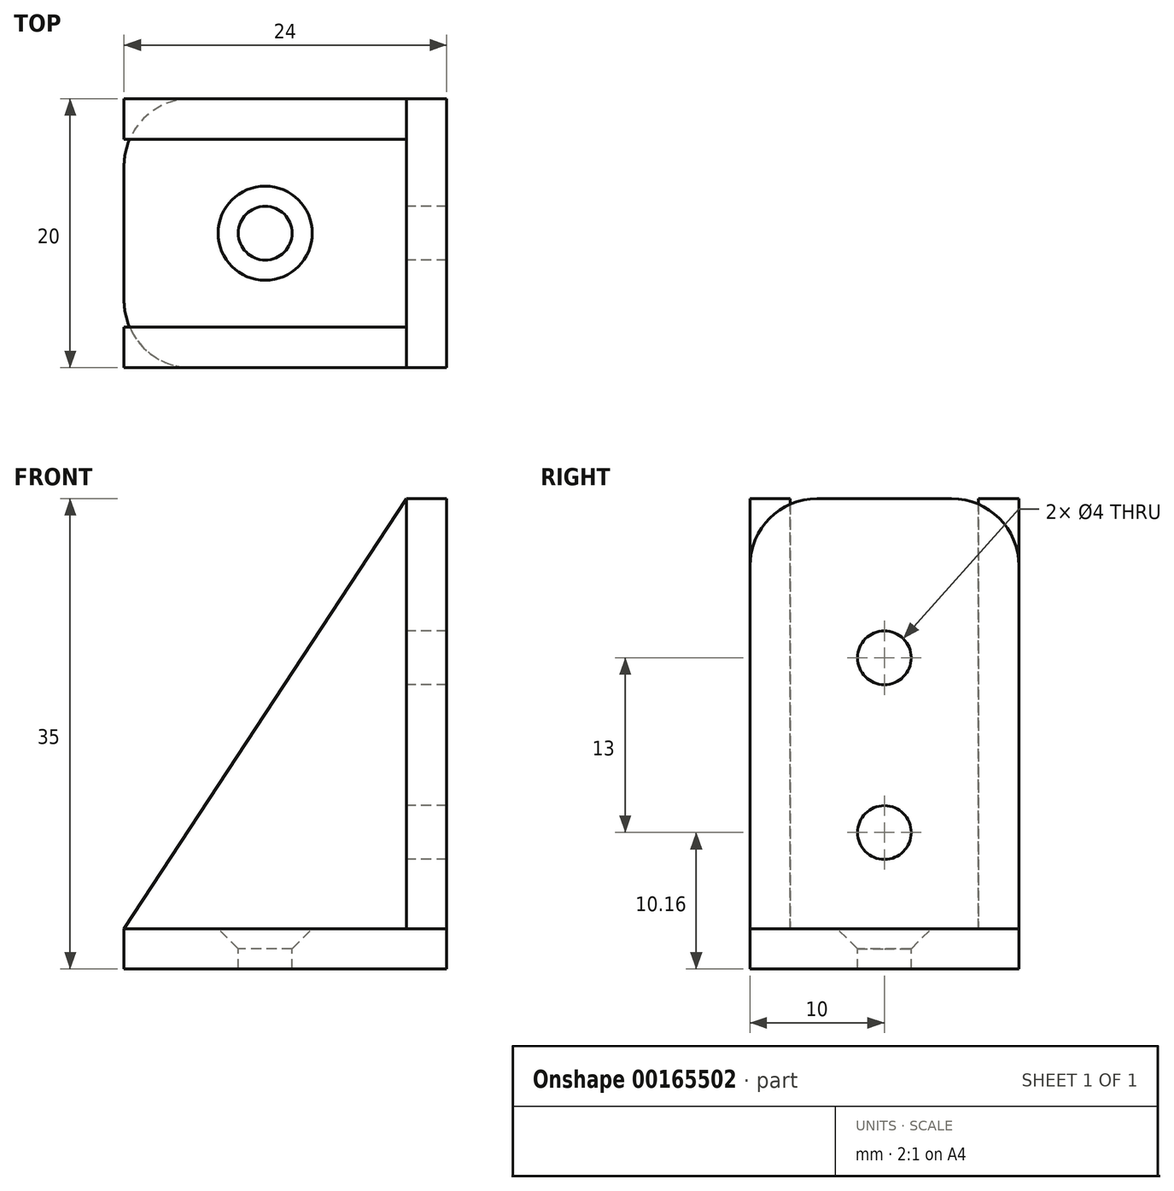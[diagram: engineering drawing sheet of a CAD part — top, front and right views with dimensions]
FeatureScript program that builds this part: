
annotation { "Feature Type Name" : "Feature", "Feature Type Description" : "" }
export const myFeature = defineFeature(function(context is Context, id is Id, definition is map)
    precondition{}
    {
        {
            var Q0;
            Q0=qCreatedBy(makeId("Top.planeOp"),FACE);
            var sketch = newSketch(context, id + "F0", { "sketchPlane" : qUnion([Q0])});
            skLineSegment(sketch, "E0", {"start": v(0, 0) * mm, "end": v(0, 10) * mm});
            skLineSegment(sketch, "E1", {"start": v(0, 10) * mm, "end": v(24, 10) * mm});
            skLineSegment(sketch, "E2", {"start": v(24, 10) * mm, "end": v(24, 0) * mm});
            skLineSegment(sketch, "E3.MirrorCS", {"start": v(0, 0) * mm, "end": v(0, -10) * mm});
            skLineSegment(sketch, "E4.MirrorCS", {"start": v(0, -10) * mm, "end": v(24, -10) * mm});
            skLineSegment(sketch, "E5.MirrorCS", {"start": v(24, -10) * mm, "end": v(24, 0) * mm});
            skSolve(sketch);
        }
        {
            var Q0;
            Q0=qSketchRegion(id+"F0",true);
            extrude(context, id + "F1", {"entities" : qUnion([Q0]), "depth" : 3 * mm});
        }
        {
            var Q0;
            Q0=makeQuery(id+"F1.opExtrude","CAP_FACE",FACE,{"disambiguationData":[OSD([sQuery(id+"F0.wireOp",EDGE,"E0"),sQuery(id+"F0.wireOp",EDGE,"E1"),sQuery(id+"F0.wireOp",EDGE,"E2"),sQuery(id+"F0.wireOp",EDGE,"E3.MirrorCS"),sQuery(id+"F0.wireOp",EDGE,"E4.MirrorCS"),sQuery(id+"F0.wireOp",EDGE,"E5.MirrorCS")])],"isStart":false});
            var sketch = newSketch(context, id + "F2", { "sketchPlane" : qUnion([Q0])});
            skLineSegment(sketch, "E6.0", {"start": v(24, -10) * mm, "end": v(24, 10) * mm});
            skLineSegment(sketch, "E6.1", {"start": v(21, 10) * mm, "end": v(24, 10) * mm});
            skLineSegment(sketch, "E6.2", {"start": v(21, -10) * mm, "end": v(24, -10) * mm});
            skLineSegment(sketch, "E7", {"start": v(21, 10) * mm, "end": v(21, -10) * mm});
            skPoint(sketch, "E8.orphan", {"position": v(0, 10) * mm});
            skPoint(sketch, "E9.orphan", {"position": v(0, -10) * mm});
            skSolve(sketch);
        }
        {
            var Q0;
            Q0=qSketchRegion(id+"F2",true);
            extrude(context, id + "F3", {"entities" : qUnion([Q0]), "depth" : 32 * mm});
        }
        {
            var Q0;
            Q0=makeQuery(id+"F1.opExtrude","SWEPT_FACE",FACE,{"disambiguationData":[OSD([sQuery(id+"F0.wireOp",EDGE,"E4.MirrorCS")])]});
            var sketch = newSketch(context, id + "F4", { "sketchPlane" : qUnion([Q0])});
            skLineSegment(sketch, "E10.0", {"start": v(21, 35) * mm, "end": v(21, 3) * mm});
            skLineSegment(sketch, "E10.1", {"start": v(0, 3) * mm, "end": v(21, 3) * mm});
            skLineSegment(sketch, "E11", {"start": v(0, 3) * mm, "end": v(21, 35) * mm});
            skPoint(sketch, "E12.orphan", {"position": v(24, 3) * mm});
            skSolve(sketch);
        }
        {
            var Q0;
            Q0=qSketchRegion(id+"F4",true);
            extrude(context, id + "F5", {"entities" : qUnion([Q0]), "oppositeDirection" : true, "depth" : 3 * mm});
        }
        {
            var Q0;
            Q0=makeQuery(id+"F5.opExtrude","SWEPT_BODY",BODY,{"disambiguationData":[OSD([sQuery(id+"F4.wireOp",EDGE,"E10.0"),sQuery(id+"F4.wireOp",EDGE,"E10.1"),sQuery(id+"F4.wireOp",EDGE,"E11")])]});
            var Q1;
            Q1=qCreatedBy(makeId("Front.planeOp"),FACE);
            mirror(context, id + "F6", {"entities" : qUnion([Q0]), "mirrorPlane" : qUnion([Q1])});
        }
        {
            var Q0;
            Q0=makeQuery(id+"F3.opExtrude","SWEPT_FACE",FACE,{"disambiguationData":[OSD([sQuery(id+"F2.wireOp",EDGE,"E7")])]});
            var sketch = newSketch(context, id + "F7", { "sketchPlane" : qUnion([Q0])});
            skPoint(sketch, "E13", {"position": v(0, 10.16) * mm});
            skPoint(sketch, "E14", {"position": v(0, 23.16) * mm});
            skSolve(sketch);
        }
        {
            var Q0;
            Q0=sQuery(id+"F7.wireOp",VERTEX,"E13");
            var Q1;
            Q1=sQuery(id+"F7.wireOp",VERTEX,"E14");
            var Q2;
            Q2=makeQuery(id+"F3.opExtrude","SWEPT_BODY",BODY,{"disambiguationData":[OSD([sQuery(id+"F2.wireOp",EDGE,"E6.0"),sQuery(id+"F2.wireOp",EDGE,"E6.1"),sQuery(id+"F2.wireOp",EDGE,"E6.2"),sQuery(id+"F2.wireOp",EDGE,"E7")])]});
            hole(context, id + "F8", {"style" : HoleStyle.SIMPLE, "endStyle" : HoleEndStyle.THROUGH, "holeDiameter" : 4 * mm, "locations" : qUnion([Q0, Q1]), "scope" : qUnion([Q2]), "isTappedThrough" : true});
        }
        {
            var Q0;
            Q0=makeQuery(id+"F1.opExtrude","CAP_FACE",FACE,{"disambiguationData":[OSD([sQuery(id+"F0.wireOp",EDGE,"E0"),sQuery(id+"F0.wireOp",EDGE,"E1"),sQuery(id+"F0.wireOp",EDGE,"E2"),sQuery(id+"F0.wireOp",EDGE,"E3.MirrorCS"),sQuery(id+"F0.wireOp",EDGE,"E4.MirrorCS"),sQuery(id+"F0.wireOp",EDGE,"E5.MirrorCS")])],"isStart":false});
            var sketch = newSketch(context, id + "F9", { "sketchPlane" : qUnion([Q0])});
            skPoint(sketch, "E15", {"position": v(10.5, 0) * mm});
            skLineSegment(sketch, "E16.0", {"start": v(21, 10) * mm, "end": v(21, -10) * mm, "construction": true});
            skLineSegment(sketch, "E16.1", {"start": v(0, 7) * mm, "end": v(21, 7) * mm, "construction": true});
            skLineSegment(sketch, "E16.2", {"start": v(0, -10) * mm, "end": v(0, 10) * mm, "construction": true});
            skLineSegment(sketch, "E16.3", {"start": v(0, -7) * mm, "end": v(21, -7) * mm, "construction": true});
            skLineSegment(sketch, "E17", {"start": v(21, 7) * mm, "end": v(0, -7) * mm, "construction": true});
            skLineSegment(sketch, "E18", {"start": v(0, 7) * mm, "end": v(21, -7) * mm, "construction": true});
            skSolve(sketch);
        }
        {
            var Q0;
            Q0=sQuery(id+"F9.wireOp",VERTEX,"E15");
            var Q1;
            Q1=makeQuery(id+"F1.opExtrude","SWEPT_BODY",BODY,{"disambiguationData":[OSD([sQuery(id+"F0.wireOp",EDGE,"E0"),sQuery(id+"F0.wireOp",EDGE,"E1"),sQuery(id+"F0.wireOp",EDGE,"E2"),sQuery(id+"F0.wireOp",EDGE,"E3.MirrorCS"),sQuery(id+"F0.wireOp",EDGE,"E4.MirrorCS"),sQuery(id+"F0.wireOp",EDGE,"E5.MirrorCS")])]});
            hole(context, id + "F10", {"style" : HoleStyle.C_SINK, "endStyle" : HoleEndStyle.THROUGH, "holeDiameter" : 4 * mm, "cSinkDiameter" : 7 * mm, "cSinkAngle" : 90 * degree, "locations" : qUnion([Q0]), "scope" : qUnion([Q1]), "isTappedThrough" : true});
        }
        {
            var Q0;
            Q0=makeQuery(id+"F1.opExtrude","SWEPT_EDGE",EDGE,{"disambiguationData":[OSD([sQuery(id+"F0.wireOp",EDGE,"E3.MirrorCS"),sQuery(id+"F0.wireOp",EDGE,"E4.MirrorCS")])]});
            var Q1;
            Q1=makeQuery(id+"F1.opExtrude","SWEPT_EDGE",EDGE,{"disambiguationData":[OSD([sQuery(id+"F0.wireOp",EDGE,"E0"),sQuery(id+"F0.wireOp",EDGE,"E1")])]});
            var Q2;
            Q2=makeQuery(id+"F3.opExtrude","CAP_EDGE",EDGE,{"disambiguationData":[OSD([sQuery(id+"F2.wireOp",EDGE,"E6.2")])],"isStart":false});
            var Q3;
            Q3=makeQuery(id+"F3.opExtrude","CAP_EDGE",EDGE,{"disambiguationData":[OSD([sQuery(id+"F2.wireOp",EDGE,"E6.1")])],"isStart":false});
            fillet(context, id + "F11", {"entities" : qUnion([Q0, Q1, Q2, Q3]), "radius" : 5 * mm, "tangentPropagation" : true, "allowEdgeOverflow" : false});
        }
    });
